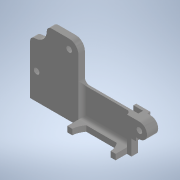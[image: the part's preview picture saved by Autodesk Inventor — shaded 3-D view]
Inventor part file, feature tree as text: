
AUTODESK INVENTOR PART (.ipt)
format: ipt  version: 2022 (Build 260153070, 153G)  size: 274,944 bytes
history: native  units: in
note: dims shown in document units (in); Inventor stores cm internally (conversion verified against a paired STEP export)
features: extrude x8, reference x7, sketch x7, other x5, fillet x1, projected_geometry x1
ambient origin geometry x8: Origin, YZ Plane, XZ Plane, XY Plane, X Axis, Y Axis, Z Axis, Center Point
bodies: Solid1 (feature_tree)
feature tree (29):
  extrude  "Extrusion1"  TaperAngle=90.0deg  [1 undecoded]
  extrude  "Extrusion2"  Depth=0.1378in
  fillet  "Fillet1"  [1 undecoded]
  extrude  "Extrusion3"  Depth=0.185in
  extrude  "Extrusion4"  Depth=0.1181in
  extrude  "Extrusion5"  Depth=0.1181in
  extrude  "Extrusion7"  Depth=0.0866in
  extrude  "Extrusion9"  Depth=0.0591in
  extrude  "Extrusion10"  Depth=0.1181in TaperAngle=0.0deg
  reference  "Reference1"
  reference  "Reference2"
  reference  "Reference4"
  reference  "Reference5"
  sketch  "Sketch2"  dims[d0=90.0deg d1=90.0deg]
  sketch  "Sketch3"  dims[d2=0.0787in d3=0.1378in d5=90.0deg]
  reference  "Reference6"
  sketch  "Sketch4"  dims[d6=90.0deg d7=0.185in]
  reference  "Reference7"
  sketch  "Sketch5"  dims[d12=0.1378in d13=0.0in d14=0.1181in]
  sketch  "Sketch8"  dims[d15=0.1181in d16=0.9843in]
  sketch  "Sketch9"  dims[d18=0.0866in d19=0.0in d21=0.0787in]
  sketch  "Sketch10"  dims[d22=0.0157in d23=0.0157in d24=0.1181in d25=0.0in d27=0.1594in d28=0.0in d30=0.1969in d31=0.0in d35=0.1181in d36=0.1024in d37=0.0689in d38=0.2362in d39=0.0in d42=0.2244in d43=0.2362in d44=0.1181in d45=0.0in d46=0.0in d47=0.0059in d48=0.3937in d49=0.0in d51=0.0984in d52=0.3937in d53=0.0984in d54=0.1181in d55=0.2559in d57=0.0591in d56=0.0344in]
  reference  "Reference10"
  projected_geometry  "Projected Loop1"
  other  "<userpath> laptop\Desktop\Another3dPrinterShroud\MODELS\ENDER 3 ASSEMBLY.iam"
  other  "ENDER 3 ASSEMBLY.iam"
  other  "ENDER 3 E_PLATE_SCREW:1"
  other  "ENDER 3 E_PLATE:1"
  other  "ENDER 3 RAD:1"
note: 2 required parameter values undecoded (feature->parameter linkage not recoverable at this tier; creation-order binding heuristic only, values carry confidence <= 0.55)
